# Revit family: Electronics_Fixed-Audio-DSP_Biamp_Tesira_TesiraFORTE_DAN-CI__
name_source: partatom
category: Communication Devices
units: mm (PartAtom-declared; Revit-internal decimal feet)

## family parameters
Cut with Voids When Loaded = No
Host = Face
Maintain Annotation Orientation = No
OmniClass Number = 23.85.10.11.11
OmniClass Title = Sound and Signal Devices
Part Type = Normal
Room Calculation Point = No
Round Connector Dimension = Use Diameter
Shared = No

## types (1)
- DAN CI
    A/D - D/A Converters = 24-bit
    Altitude = 0-6,600 ft (0-2000m) MSL
    Apparent Load = 35 VA
    Bit Depth = 16- or 24-bit
    Compliance = FCC Part 15B (USA), CE marked (Europe), UL und C-UL listed (USA and Canada), RCM (Australia), RoHS Directive (Europe)
    Connector Description = 100-240VAC 50/60Hz
    Cross Talk = 0dB gain, +4dBu input: < -85dB; 54dB gain, -50dBu input: < -75dB
    DAN/AVB = Yes
    Default Elevation = 48 "
    Depth = 10.5 "
    Description = TesiraFORTÉ® DAN CI Fixed I/O DSP
    Dynamic Range = 22Hz to 22kHz, 0dB gain: > 108dB
    EIN = no weighting, 22Hz to 22kHz: < -125dBu
    Frequency Response = 20Hz to 20kHz, +4dBu output: +0.25 dB/-0.5 dB
    Height = 1.75 "
    Housing Material = Biamp - Metal - Silver
    Humidity = 0-98% relative humidity (non-condensing)
    Input Gain Range = 0-66dB
    Input Impedance = 8 kohm
    Manufacturer = Biamp
    Max Power Consumption = 35 W
    Maximum Input = +24dBu
    Maximum Output = +24dBu, +18dBu, +12dBu, +6dBu, 0dBu, -31dBu
    Model = TesiraFORTÉ DAN CI
    Number of Channels = up to 8
    Number of Poles = 1
    Output Impedance = 207 ohm
    Phantom Power = +48VDC (7mA/input)
    Power Factor = 1
    Product Documentation Link = https://downloads.biamp.com
    Product Page URL = https://www.biamp.com
    Product data url = https://www.bimobject.com
    Sample Rate = USB 48kHz
    Sampling Rate = 48kHz
    THD+N = 0dB gain, +4dBu input: < 0.006%; 54dB gain, -50dBu input: < 0.040%
    Temperature Range = 32 - 104° F (0 - 40° C)
    Type 2 = Yes
    Type1 = Yes
    URL = https://www.biamp.com
    VoIP+Telephone Line = No
    Voltage = 120 V
    Weight = 8.00 lbf
    Width = 19 "

## geometry (parser evidence)
native form markers: Sweep x2
no freeform markers — native parametric forms only
